# Revit family: Sanitary_Mirrors_Sloan-Valve_MF-Angle-Framew
name_source: partatom
category: Furniture
units: mm (PartAtom-declared; Revit-internal decimal feet)

## family parameters
Cut with Voids When Loaded = No
Host = Face
OmniClass Number = 23.40.95.17.17
OmniClass Title = Mirrors
Room Calculation Point = No
Shared = No

## types (6) — shared parameters
Custom Size Note = Please reach out to Sloan Valve Company for information on custom sizes.
Default Elevation = 48"
Depth = 1"
Height = 36"
Manufacturer = Sloan Valve
Product data url = https://bimobject.com
Real Height = 36"
URL = www.sloanvalve.com
Version = 1
z_Case Back Height = 35 1/2"
z_Cutout Height = 2 1/2"
z_Cutout Width = 1 1/2"
z_Wall Panel Left Offset = 1 1/2"
z_Wall Panel Top Offset = 1"
z_Wall Panel Width 1 = 2"
z_Wall Panel Width 2 = 1 1/2"

## per-type parameters (varying)
| type | Description | Part Number | Product Material | Real Width | Weight | Width | z_Case Back Width |
| MF Angle Frame-18x36-BN | 18" x 36", Brushed Nickel, Sloan 11/16" Wall-hung Angle Frame Mirror. | 32910028 | Sloan Valve - Finish - Brushed Nickel | 18" | 28.00 lbf | 18" | 17 1/2" |
| MF Angle Frame-24x36-CP | 24" x 36", Polished Chrome, Sloan 11/16" Wall-hung Angle Frame Mirror. | 32910015 | Sloan Valve - Finish - Polished Chrome | 24" | 36.00 lbf | 24" | 23 1/2" |
| MF Angle Frame-24x36-GR | 24" x 36", Graphite, Sloan 11/16" Wall-hung Angle Frame Mirror. | 32910011 | Sloan Valve - Finish - Graphite | 24" | 36.00 lbf | 24" | 23 1/2" |
| MF Angle Frame-18x36-GR | 18" x 36", Graphite, Sloan 11/16" Wall-hung Angle Frame Mirror. | 32910026 | Sloan Valve - Finish - Graphite | 18" | 28.00 lbf | 18" | 17 1/2" |
| MF Angle Frame-24x36-BN | 24" x 36", Brushed Nickel, Sloan 11/16" Wall-hung Angle Frame Mirror. | 32910013 | Sloan Valve - Finish - Brushed Nickel | 24" | 36.00 lbf | 24" | 23 1/2" |
| MF Angle Frame-18x36-CP | 18" x 36", Polished Chrome, Sloan 11/16" Wall-hung Angle Frame Mirror. | 32910030 | Sloan Valve - Finish - Polished Chrome | 18" | 28.00 lbf | 18" | 17 1/2" |

note: column(s) folded — value = type name in every type: Model

## geometry (parser evidence)
native form markers: Sweep x2
no freeform markers — native parametric forms only
